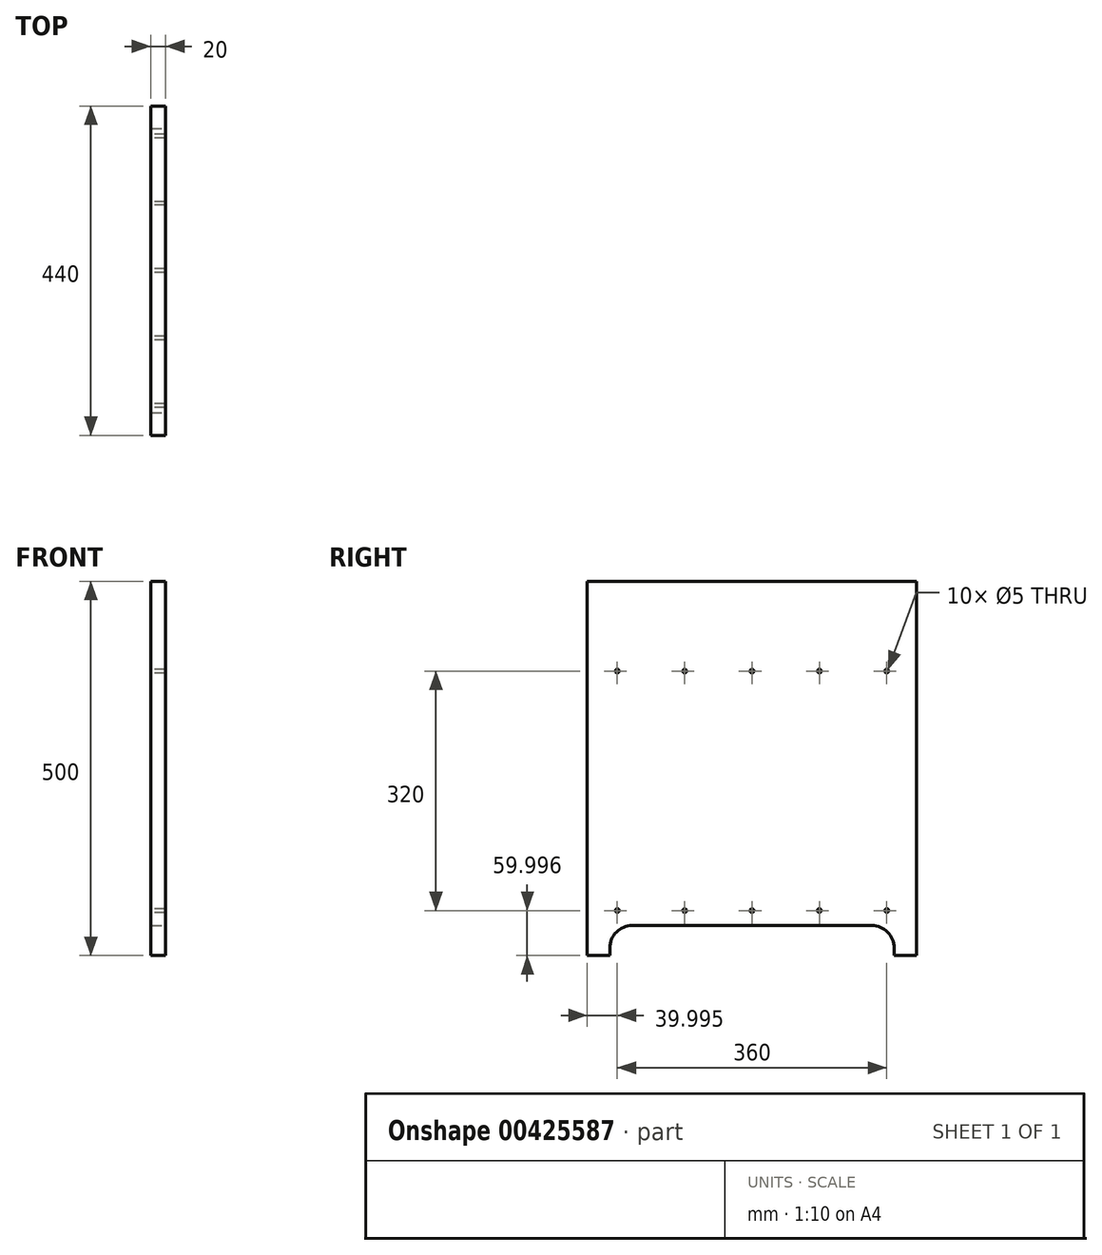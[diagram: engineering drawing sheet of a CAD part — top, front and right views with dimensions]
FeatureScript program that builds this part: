
annotation { "Feature Type Name" : "Feature", "Feature Type Description" : "" }
export const myFeature = defineFeature(function(context is Context, id is Id, definition is map)
    precondition{}
    {
        {
            var Q0;
            Q0=qCreatedBy(makeId("Right.planeOp"),FACE);
            var sketch = newSketch(context, id + "F0", { "sketchPlane" : qUnion([Q0])});
            skLineSegment(sketch, "E0.bottom", {"start": v(-188.64, 256.57) * mm, "end": v(251.36, 256.57) * mm});
            skLineSegment(sketch, "E0.top", {"start": v(-188.64, -243.43) * mm, "end": v(251.36, -243.43) * mm});
            skLineSegment(sketch, "E0.left", {"start": v(-188.64, 256.57) * mm, "end": v(-188.64, -243.43) * mm});
            skLineSegment(sketch, "E0.right", {"start": v(251.36, 256.57) * mm, "end": v(251.36, -243.43) * mm});
            skSolve(sketch);
        }
        {
            var Q0;
            Q0 = qSketchRegion(id + "F0", true);
            extrude(context, id + "F1", {"entities" : qUnion([Q0]), "depth" : 20 * mm});
        }
        {
            var Q0;
            Q0=makeQuery(id+"F1.opExtrude","CAP_FACE",FACE,{"disambiguationData":[OSD([sQuery(id+"F0.wireOp",EDGE,"E0.bottom"),sQuery(id+"F0.wireOp",EDGE,"E0.top"),sQuery(id+"F0.wireOp",EDGE,"E0.left"),sQuery(id+"F0.wireOp",EDGE,"E0.right")])],"isStart":false});
            var sketch = newSketch(context, id + "F2", { "sketchPlane" : qUnion([Q0])});
            skPoint(sketch, "E1.oppositeSnap0", {"position": v(31.36, -243.43) * mm});
            skLineSegment(sketch, "E1.bottom", {"start": v(-158.64, -243.43) * mm, "end": v(31.36, -243.43) * mm});
            skLineSegment(sketch, "E1.top", {"start": v(-158.64, -203.43) * mm, "end": v(31.36, -203.43) * mm});
            skLineSegment(sketch, "E1.left", {"start": v(-158.64, -243.43) * mm, "end": v(-158.64, -203.43) * mm});
            skLineSegment(sketch, "E1.right", {"start": v(31.36, -243.43) * mm, "end": v(31.36, -203.43) * mm});
            skLineSegment(sketch, "E2.MirrorCS", {"start": v(221.36, -243.43) * mm, "end": v(221.36, -203.43) * mm});
            skLineSegment(sketch, "E3.MirrorCS", {"start": v(221.36, -203.43) * mm, "end": v(31.36, -203.43) * mm});
            skLineSegment(sketch, "E4.MirrorCS", {"start": v(221.36, -243.43) * mm, "end": v(31.36, -243.43) * mm});
            skSolve(sketch);
        }
        {
            var Q0;
            Q0 = qSketchRegion(id + "F2", true);
            extrude(context, id + "F3", {"entities" : qUnion([Q0]), "operationType" : NewBodyOperationType.REMOVE, "endBound" : BoundingType.UP_TO_NEXT, "oppositeDirection" : true, "depth" : 25 * mm});
        }
        {
            var Q0;
            Q0=makeQuery(id+"F3.boolean.opBoolean","COPY",EDGE,{"derivedFrom":makeQuery(id+"F3.opExtrude","SWEPT_EDGE",EDGE,{"disambiguationData":[OSD([sQuery(id+"F2.wireOp",EDGE,"E1.top"),sQuery(id+"F2.wireOp",EDGE,"E1.left")])]})});
            var Q1;
            Q1=makeQuery(id+"F3.boolean.opBoolean","COPY",EDGE,{"derivedFrom":makeQuery(id+"F3.opExtrude","SWEPT_EDGE",EDGE,{"disambiguationData":[OSD([sQuery(id+"F2.wireOp",EDGE,"E2.MirrorCS"),sQuery(id+"F2.wireOp",EDGE,"E3.MirrorCS")])]})});
            fillet(context, id + "F4", {"entities" : qUnion([Q0, Q1]), "radius" : 30 * mm, "tangentPropagation" : true, "allowEdgeOverflow" : false});
        }
        {
            var Q0;
            Q0=makeQuery(id+"F1.opExtrude","CAP_FACE",FACE,{"disambiguationData":[OSD([sQuery(id+"F0.wireOp",EDGE,"E0.bottom"),sQuery(id+"F0.wireOp",EDGE,"E0.top"),sQuery(id+"F0.wireOp",EDGE,"E0.left"),sQuery(id+"F0.wireOp",EDGE,"E0.right")])],"isStart":true});
            var sketch = newSketch(context, id + "F5", { "sketchPlane" : qUnion([Q0])});
            skPoint(sketch, "E5", {"position": v(-211.36, -183.43) * mm});
            skPoint(sketch, "E6", {"position": v(-121.36, -183.43) * mm});
            skPoint(sketch, "E7", {"position": v(-31.36, -183.43) * mm});
            skPoint(sketch, "E8", {"position": v(58.64, -183.43) * mm});
            skPoint(sketch, "E9", {"position": v(148.64, -183.43) * mm});
            skLineSegment(sketch, "E10", {"start": v(-31.36, 256.57) * mm, "end": v(-31.36, -203.43) * mm});
            skPoint(sketch, "E11", {"position": v(148.64, 136.57) * mm});
            skPoint(sketch, "E12", {"position": v(58.64, 136.57) * mm});
            skPoint(sketch, "E13", {"position": v(-31.36, 136.57) * mm});
            skPoint(sketch, "E14", {"position": v(-121.36, 136.57) * mm});
            skPoint(sketch, "E15", {"position": v(-211.36, 136.57) * mm});
            skSolve(sketch);
        }
        {
            var Q0;
            Q0=sQuery(id+"F5.wireOp",VERTEX,"24f7d3bb-b01e-4e0f-b29a-86b1a1f706cc0.MirrorP");
            var Q1;
            Q1=sQuery(id+"F5.wireOp",VERTEX,"390eda45-e8fa-4d78-9c98-413c1594fdba0.MirrorP");
            var Q2;
            Q2=sQuery(id+"F5.wireOp",VERTEX,"d84ee400-2526-4680-88ac-f5700c33950b0.MirrorP");
            var Q3;
            Q3=sQuery(id+"F5.wireOp",VERTEX,"66b6a51f-8bd4-4044-a3a9-3e9e5ba87f6c0.MirrorP");
            var Q4;
            Q4=sQuery(id+"F5.wireOp",VERTEX,"e36e9a4a-0bf2-480b-b309-26bd45dee6470.MirrorP");
            var Q5;
            Q5=sQuery(id+"F5.wireOp",VERTEX,"E9");
            var Q6;
            Q6=sQuery(id+"F5.wireOp",VERTEX,"E8");
            var Q7;
            Q7=sQuery(id+"F5.wireOp",VERTEX,"E7");
            var Q8;
            Q8=sQuery(id+"F5.wireOp",VERTEX,"E6");
            var Q9;
            Q9=sQuery(id+"F5.wireOp",VERTEX,"E5");
            var Q10;
            Q10=sQuery(id+"F5.wireOp",VERTEX,"E11");
            var Q11;
            Q11=sQuery(id+"F5.wireOp",VERTEX,"E12");
            var Q12;
            Q12=sQuery(id+"F5.wireOp",VERTEX,"E13");
            var Q13;
            Q13=sQuery(id+"F5.wireOp",VERTEX,"E14");
            var Q14;
            Q14=sQuery(id+"F5.wireOp",VERTEX,"E15");
            var Q15;
            Q15=makeQuery(id+"F1.opExtrude","SWEPT_BODY",BODY,{"disambiguationData":[OSD([sQuery(id+"F0.wireOp",EDGE,"E0.bottom"),sQuery(id+"F0.wireOp",EDGE,"E0.top"),sQuery(id+"F0.wireOp",EDGE,"E0.left"),sQuery(id+"F0.wireOp",EDGE,"E0.right")])]});
            hole(context, id + "F6", {"style" : HoleStyle.SIMPLE, "endStyle" : HoleEndStyle.THROUGH, "holeDiameter" : 5 * mm, "isTappedThrough" : true, "tappedDepth" : 12 * mm, "tapClearance" : 3, "locations" : qUnion([Q0, Q1, Q2, Q3, Q4, Q5, Q6, Q7, Q8, Q9, Q10, Q11, Q12, Q13, Q14]), "scope" : qUnion([Q15])});
        }
    });
